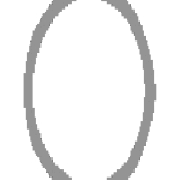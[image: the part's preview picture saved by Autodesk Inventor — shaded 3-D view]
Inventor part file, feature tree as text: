
AUTODESK INVENTOR PART (.ipt)
format: ipt  version: 2021 (Build 250183000, 183)  size: 115,200 bytes
history: native  units: in
note: dims shown in document units (in); Inventor stores cm internally (conversion verified against a paired STEP export)
features: other x4, sketch x3, plane x1
ambient origin geometry x8: Origin, YZ Plane, XZ Plane, XY Plane, X Axis, Y Axis, Z Axis, Center Point
bodies: Solid1 (feature_tree), Body (feature_tree)
feature tree (8):
  other  "Driven Length"
  other  "Frame Generator"
  other  "Start Plane"
  other  "End Plane"
  sketch  "Sketch"  dims[d2=6.0in d4=-0.0in d5=6.0in d6=0.12in d7=0.0in d8=90.0deg d9=6.0in]
  sketch  "Sketch2"  dims[d0=1.0in]
  plane  "Work Plane3"
  sketch  "Sketch3"  dims[d1=0.065in]
